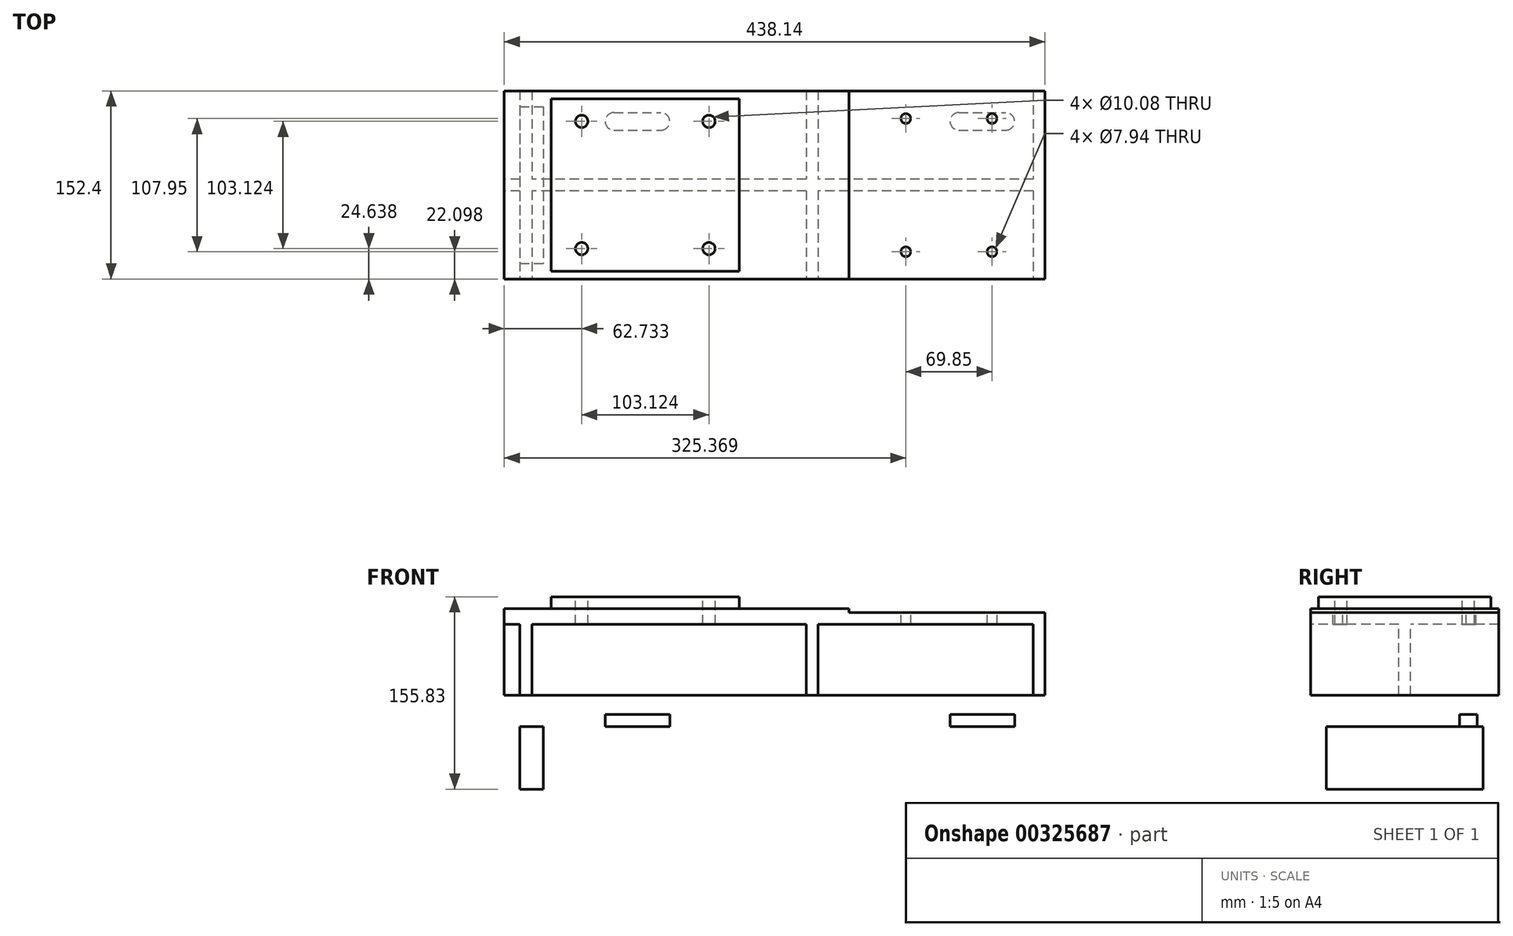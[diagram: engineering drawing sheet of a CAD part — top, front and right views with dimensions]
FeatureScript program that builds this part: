
annotation { "Feature Type Name" : "Feature", "Feature Type Description" : "" }
export const myFeature = defineFeature(function(context is Context, id is Id, definition is map)
    precondition{}
    {
        {
            var Q0;
            Q0=qCreatedBy(makeId("Top.planeOp"),FACE);
            var sketch = newSketch(context, id + "F0", { "sketchPlane" : qUnion([Q0])});
            skLineSegment(sketch, "E0.bottom", {"start": v(-219.08, 76.2) * mm, "end": v(219.08, 76.2) * mm});
            skLineSegment(sketch, "E0.top", {"start": v(-219.08, -76.2) * mm, "end": v(219.07, -76.2) * mm});
            skLineSegment(sketch, "E0.left", {"start": v(-219.08, 76.2) * mm, "end": v(-219.08, -76.2) * mm});
            skLineSegment(sketch, "E0.right", {"start": v(219.08, 76.2) * mm, "end": v(219.07, -76.2) * mm});
            skPoint(sketch, "E0.middle", {"position": v(0, 0) * mm});
            skSolve(sketch);
        }
        {
            var Q0;
            Q0=qSketchRegion(id+"F0",true);
            extrude(context, id + "F1", {"entities" : qUnion([Q0]), "oppositeDirection" : true, "depth" : 12.7 * mm});
        }
        {
            var Q0;
            Q0=makeQuery(id+"F1.opExtrude","CAP_FACE",FACE,{"disambiguationData":[OSD([sQuery(id+"F0.wireOp",EDGE,"E0.bottom"),sQuery(id+"F0.wireOp",EDGE,"E0.top"),sQuery(id+"F0.wireOp",EDGE,"E0.left"),sQuery(id+"F0.wireOp",EDGE,"E0.right")])],"isStart":true});
            var sketch = newSketch(context, id + "F2", { "sketchPlane" : qUnion([Q0])});
            skLineSegment(sketch, "E1.0", {"start": v(-104.78, 76.2) * mm, "end": v(-104.78, -76.2) * mm, "construction": true});
            skLineSegment(sketch, "E2.bottom", {"start": v(-180.98, -69.85) * mm, "end": v(-28.58, -69.85) * mm});
            skLineSegment(sketch, "E2.top", {"start": v(-180.98, 69.85) * mm, "end": v(-28.58, 69.85) * mm});
            skLineSegment(sketch, "E2.left", {"start": v(-180.98, -69.85) * mm, "end": v(-180.98, 69.85) * mm});
            skLineSegment(sketch, "E2.right", {"start": v(-28.58, -69.85) * mm, "end": v(-28.58, 69.85) * mm});
            skPoint(sketch, "E2.middle", {"position": v(-104.78, 0) * mm});
            skSolve(sketch);
        }
        {
            var Q0;
            Q0=qSketchRegion(id+"F2",true);
            extrude(context, id + "F3", {"entities" : qUnion([Q0]), "operationType" : NewBodyOperationType.ADD, "depth" : 9.52 * mm});
        }
        {
            var Q0;
            Q0=makeQuery(id+"F1.opExtrude","CAP_FACE",FACE,{"disambiguationData":[OSD([sQuery(id+"F0.wireOp",EDGE,"E0.bottom"),sQuery(id+"F0.wireOp",EDGE,"E0.top"),sQuery(id+"F0.wireOp",EDGE,"E0.left"),sQuery(id+"F0.wireOp",EDGE,"E0.right")])],"isStart":false});
            var sketch = newSketch(context, id + "F4", { "sketchPlane" : qUnion([Q0])});
            skLineSegment(sketch, "E3.0", {"start": v(-206.38, 76.2) * mm, "end": v(-196.72, 76.2) * mm});
            skLineSegment(sketch, "E4.0", {"start": v(-206.38, -76.2) * mm, "end": v(-196.72, -76.2) * mm});
            skLineSegment(sketch, "E5.0", {"start": v(-206.38, -76.2) * mm, "end": v(-206.38, 76.2) * mm});
            skLineSegment(sketch, "E6.0", {"start": v(-196.72, -76.2) * mm, "end": v(-196.72, 76.2) * mm});
            skLineSegment(sketch, "E7.0", {"start": v(25.53, -76.2) * mm, "end": v(25.53, 76.2) * mm});
            skLineSegment(sketch, "E8.0", {"start": v(35.18, -76.2) * mm, "end": v(35.18, 76.2) * mm});
            skLineSegment(sketch, "E9.0", {"start": v(219.08, -76.2) * mm, "end": v(219.07, 76.2) * mm});
            skLineSegment(sketch, "E10.0", {"start": v(209.42, -76.2) * mm, "end": v(209.42, 76.2) * mm});
            skLineSegment(sketch, "E11", {"start": v(219.08, 0) * mm, "end": v(-321.3, 0) * mm, "construction": true});
            skPoint(sketch, "E11.endSnap0", {"position": v(219.07, 0) * mm});
            skLineSegment(sketch, "E12.0", {"start": v(219.08, 4.76) * mm, "end": v(-219.08, 4.76) * mm});
            skLineSegment(sketch, "E13.MirrorCS", {"start": v(219.08, -4.76) * mm, "end": v(-219.08, -4.76) * mm});
            skLineSegment(sketch, "E14.0", {"start": v(-219.08, -4.76) * mm, "end": v(-219.08, 4.76) * mm});
            skPoint(sketch, "E15.orphan", {"position": v(-219.08, 76.2) * mm});
            skPoint(sketch, "E16.orphan", {"position": v(-321.3, 4.76) * mm});
            skPoint(sketch, "E17.orphan", {"position": v(-321.3, -4.76) * mm});
            skPoint(sketch, "E18.orphan", {"position": v(-219.08, -76.2) * mm});
            skLineSegment(sketch, "E19.trimOffspring", {"start": v(25.53, -76.2) * mm, "end": v(35.18, -76.2) * mm});
            skLineSegment(sketch, "E20.trimOffspring", {"start": v(25.53, 76.2) * mm, "end": v(35.18, 76.2) * mm});
            skLineSegment(sketch, "E21.trimOffspring", {"start": v(209.42, 76.2) * mm, "end": v(219.07, 76.2) * mm});
            skLineSegment(sketch, "E22.trimOffspring", {"start": v(209.42, -76.2) * mm, "end": v(219.08, -76.2) * mm});
            skSolve(sketch);
        }
        {
            var Q0;
            Q0=qSketchRegion(id+"F4",true);
            extrude(context, id + "F5", {"entities" : qUnion([Q0]), "operationType" : NewBodyOperationType.ADD, "depth" : 73.15 * mm});
        }
        {
            var Q0;
            Q0=makeQuery(id+"F5.opExtrude","CAP_FACE",FACE,{"disambiguationData":[OSD([sQuery(id+"F4.wireOp",EDGE,"E3.0"),sQuery(id+"F4.wireOp",EDGE,"E4.0"),sQuery(id+"F4.wireOp",EDGE,"E5.0"),sQuery(id+"F4.wireOp",EDGE,"E6.0"),sQuery(id+"F4.wireOp",EDGE,"E7.0"),sQuery(id+"F4.wireOp",EDGE,"E8.0"),sQuery(id+"F4.wireOp",EDGE,"E9.0"),sQuery(id+"F4.wireOp",EDGE,"E10.0"),sQuery(id+"F4.wireOp",EDGE,"E12.0"),sQuery(id+"F4.wireOp",EDGE,"E13.MirrorCS"),sQuery(id+"F4.wireOp",EDGE,"E14.0"),sQuery(id+"F4.wireOp",EDGE,"E19.trimOffspring"),sQuery(id+"F4.wireOp",EDGE,"E20.trimOffspring"),sQuery(id+"F4.wireOp",EDGE,"E21.trimOffspring"),sQuery(id+"F4.wireOp",EDGE,"E22.trimOffspring")])],"isStart":false});
            var sketch = newSketch(context, id + "F6", { "sketchPlane" : qUnion([Q0])});
            skLineSegment(sketch, "E23.0", {"start": v(-219.08, 76.2) * mm, "end": v(219.07, 76.2) * mm});
            skLineSegment(sketch, "E24.0", {"start": v(-219.08, -76.2) * mm, "end": v(-219.08, 76.2) * mm});
            skLineSegment(sketch, "E25.0", {"start": v(-219.08, -76.2) * mm, "end": v(219.08, -76.2) * mm});
            skLineSegment(sketch, "E26.0", {"start": v(219.08, -76.2) * mm, "end": v(219.07, 76.2) * mm});
            skPoint(sketch, "E27.orphan", {"position": v(-219.08, -4.76) * mm});
            skPoint(sketch, "E28.orphan", {"position": v(-196.72, 76.2) * mm});
            skPoint(sketch, "E29.orphan", {"position": v(25.53, 76.2) * mm});
            skPoint(sketch, "E30.orphan", {"position": v(-196.72, -76.2) * mm});
            skPoint(sketch, "E31.orphan", {"position": v(25.53, -76.2) * mm});
            skSolve(sketch);
        }
        {
            var Q0;
            Q0=qSketchRegion(id+"F6",true);
            extrude(context, id + "F7", {"entities" : qUnion([Q0]), "operationType" : NewBodyOperationType.ADD, "depth" : 9.65 * mm});
        }
        {
            var Q0;
            Q0=makeQuery(id+"F7.opExtrude","CAP_FACE",FACE,{"disambiguationData":[OSD([sQuery(id+"F6.wireOp",EDGE,"E23.0"),sQuery(id+"F6.wireOp",EDGE,"E24.0"),sQuery(id+"F6.wireOp",EDGE,"E25.0"),sQuery(id+"F6.wireOp",EDGE,"E26.0")])],"isStart":false});
            var sketch = newSketch(context, id + "F8", { "sketchPlane" : qUnion([Q0])});
            skLineSegment(sketch, "E32", {"start": v(-219.08, 0) * mm, "end": v(219.07, 0) * mm, "construction": true});
            skLineSegment(sketch, "E33.0", {"start": v(-130.18, -76.2) * mm, "end": v(-130.18, 76.2) * mm, "construction": true});
            skLineSegment(sketch, "E34.0", {"start": v(-92.08, -76.2) * mm, "end": v(-92.08, 76.2) * mm, "construction": true});
            skLineSegment(sketch, "E35.0", {"start": v(149.22, -76.2) * mm, "end": v(149.22, 76.2) * mm, "construction": true});
            skLineSegment(sketch, "E36.0", {"start": v(187.32, -76.2) * mm, "end": v(187.32, 76.2) * mm, "construction": true});
            skLineSegment(sketch, "E37.0", {"start": v(-130.18, -51.56) * mm, "end": v(-92.08, -51.56) * mm});
            skLineSegment(sketch, "E38.trimOffspring", {"start": v(149.22, -51.56) * mm, "end": v(187.32, -51.56) * mm});
            skArc(sketch, "E39.0.startCap", {"start": v(-130.18, -58.67) * mm, "mid": v(-137.29, -51.56) * mm, "end": v(-130.18, -44.45) * mm});
            skArc(sketch, "E39.0.endCap", {"start": v(-92.08, -44.45) * mm, "mid": v(-84.96, -51.56) * mm, "end": v(-92.08, -58.67) * mm});
            skLineSegment(sketch, "E39.0.left", {"start": v(-130.18, -44.45) * mm, "end": v(-92.08, -44.45) * mm});
            skLineSegment(sketch, "E39.0.right", {"start": v(-130.18, -58.67) * mm, "end": v(-92.08, -58.67) * mm});
            skArc(sketch, "E39.1.startCap", {"start": v(149.22, -58.67) * mm, "mid": v(142.11, -51.56) * mm, "end": v(149.22, -44.45) * mm});
            skArc(sketch, "E39.1.endCap", {"start": v(187.32, -44.45) * mm, "mid": v(194.44, -51.56) * mm, "end": v(187.32, -58.67) * mm});
            skLineSegment(sketch, "E39.1.left", {"start": v(149.22, -44.45) * mm, "end": v(187.32, -44.45) * mm});
            skLineSegment(sketch, "E39.1.right", {"start": v(149.22, -58.67) * mm, "end": v(187.32, -58.67) * mm});
            skArc(sketch, "E40.MirrorCS", {"start": v(-92.08, 44.45) * mm, "mid": v(-84.96, 51.56) * mm, "end": v(-92.08, 58.67) * mm});
            skArc(sketch, "E41.MirrorCS", {"start": v(-130.18, 58.67) * mm, "mid": v(-137.29, 51.56) * mm, "end": v(-130.18, 44.45) * mm});
            skLineSegment(sketch, "E42.MirrorCS", {"start": v(149.22, 51.56) * mm, "end": v(187.32, 51.56) * mm});
            skLineSegment(sketch, "E43.MirrorCS", {"start": v(-130.18, 51.56) * mm, "end": v(-92.08, 51.56) * mm});
            skLineSegment(sketch, "E44.MirrorCS", {"start": v(149.22, 58.67) * mm, "end": v(187.32, 58.67) * mm});
            skLineSegment(sketch, "E45.MirrorCS", {"start": v(-130.18, 44.45) * mm, "end": v(-92.08, 44.45) * mm});
            skLineSegment(sketch, "E46.MirrorCS", {"start": v(149.22, 44.45) * mm, "end": v(187.32, 44.45) * mm});
            skArc(sketch, "E47.MirrorCS", {"start": v(149.22, 58.67) * mm, "mid": v(142.11, 51.56) * mm, "end": v(149.22, 44.45) * mm});
            skArc(sketch, "E48.MirrorCS", {"start": v(187.32, 44.45) * mm, "mid": v(194.44, 51.56) * mm, "end": v(187.32, 58.67) * mm});
            skLineSegment(sketch, "E49.MirrorCS", {"start": v(-130.18, 58.67) * mm, "end": v(-92.08, 58.67) * mm});
            skSolve(sketch);
        }
        {
            var Q0;
            Q0=makeQuery(id+"F8.imprint","IMPRINT",FACE,{"disambiguationData":[TD([[makeQuery(id+"F8.imprint","IMPRINT",EDGE,{"derivedFrom":sQuery(id+"F8.wireOp",EDGE,"E40.MirrorCS")}),1.0]])]});
            var Q1;
            Q1=makeQuery(id+"F8.imprint","IMPRINT",FACE,{"disambiguationData":[TD([[makeQuery(id+"F8.imprint","IMPRINT",EDGE,{"derivedFrom":sQuery(id+"F8.wireOp",EDGE,"E39.0.startCap")}),-1.0]])]});
            var Q2;
            Q2=makeQuery(id+"F8.imprint","IMPRINT",FACE,{"disambiguationData":[TD([[makeQuery(id+"F8.imprint","IMPRINT",EDGE,{"derivedFrom":sQuery(id+"F8.wireOp",EDGE,"E44.MirrorCS")}),-1.0]])]});
            var Q3;
            Q3=makeQuery(id+"F8.imprint","IMPRINT",FACE,{"disambiguationData":[TD([[makeQuery(id+"F8.imprint","IMPRINT",EDGE,{"derivedFrom":sQuery(id+"F8.wireOp",EDGE,"E39.1.startCap")}),-1.0]])]});
            extrude(context, id + "F9", {"entities" : qUnion([Q0, Q1, Q2, Q3]), "operationType" : NewBodyOperationType.REMOVE, "oppositeDirection" : true, "depth" : 25.4 * mm});
        }
        {
            var Q0;
            Q0=makeQuery(id+"F3.opExtrude","CAP_FACE",FACE,{"disambiguationData":[OSD([sQuery(id+"F2.wireOp",EDGE,"E2.bottom"),sQuery(id+"F2.wireOp",EDGE,"E2.top"),sQuery(id+"F2.wireOp",EDGE,"E2.left"),sQuery(id+"F2.wireOp",EDGE,"E2.right")])],"isStart":false});
            var sketch = newSketch(context, id + "F10", { "sketchPlane" : qUnion([Q0])});
            skLineSegment(sketch, "E50.0", {"start": v(-180.98, 69.85) * mm, "end": v(-28.58, 69.85) * mm, "construction": true});
            skLineSegment(sketch, "E51.0", {"start": v(-180.98, -69.85) * mm, "end": v(-180.98, 69.85) * mm, "construction": true});
            skLineSegment(sketch, "E52.0", {"start": v(-180.98, -69.85) * mm, "end": v(-28.58, -69.85) * mm, "construction": true});
            skLineSegment(sketch, "E53", {"start": v(-28.58, -69.85) * mm, "end": v(-180.97, 69.85) * mm, "construction": true});
            skLineSegment(sketch, "E54.bottom", {"start": v(-156.34, 51.56) * mm, "end": v(-53.21, 51.56) * mm, "construction": true});
            skLineSegment(sketch, "E54.top", {"start": v(-156.34, -51.56) * mm, "end": v(-53.21, -51.56) * mm, "construction": true});
            skLineSegment(sketch, "E54.left", {"start": v(-156.34, 51.56) * mm, "end": v(-156.34, -51.56) * mm, "construction": true});
            skLineSegment(sketch, "E54.right", {"start": v(-53.21, 51.56) * mm, "end": v(-53.21, -51.56) * mm, "construction": true});
            skPoint(sketch, "E54.middle", {"position": v(-104.78, 0) * mm});
            skPoint(sketch, "E55", {"position": v(-156.34, 51.56) * mm});
            skPoint(sketch, "E56", {"position": v(-53.21, 51.56) * mm});
            skPoint(sketch, "E57", {"position": v(-156.34, -51.56) * mm});
            skPoint(sketch, "E58", {"position": v(-53.21, -51.56) * mm});
            skSolve(sketch);
        }
        {
            var Q0;
            Q0=sQuery(id+"F10.wireOp",VERTEX,"E55");
            var Q1;
            Q1=sQuery(id+"F10.wireOp",VERTEX,"E56");
            var Q2;
            Q2=sQuery(id+"F10.wireOp",VERTEX,"E57");
            var Q3;
            Q3=sQuery(id+"F10.wireOp",VERTEX,"E58");
            var Q4;
            Q4=makeQuery(id+"F1.opExtrude","SWEPT_BODY",BODY,{"disambiguationData":[OSD([sQuery(id+"F0.wireOp",EDGE,"E0.bottom"),sQuery(id+"F0.wireOp",EDGE,"E0.top"),sQuery(id+"F0.wireOp",EDGE,"E0.left"),sQuery(id+"F0.wireOp",EDGE,"E0.right")])]});
            hole(context, id + "F11", {"style" : HoleStyle.SIMPLE, "endStyle" : HoleEndStyle.BLIND, "standardTappedOrClearance" : lookupTablePath({ "standard" : "ANSI", "fit" : "Normal (ASME)", "size" : "3/8", "type" : "Clearance" }), "standardBlindInLast" : lookupTablePath({ "fit" : "Free", "standard" : "ANSI", "size" : "3/8", "type" : "Clearance" }), "holeDiameter" : 10.08 * mm, "holeDepth" : 38.1 * mm, "tappedDepth" : 14.3 * mm, "tapClearance" : 3, "locations" : qUnion([Q0, Q1, Q2, Q3]), "scope" : qUnion([Q4])});
        }
        {
            var Q0;
            Q0=makeQuery(id+"F1.opExtrude","CAP_FACE",FACE,{"disambiguationData":[OSD([sQuery(id+"F0.wireOp",EDGE,"E0.bottom"),sQuery(id+"F0.wireOp",EDGE,"E0.top"),sQuery(id+"F0.wireOp",EDGE,"E0.left"),sQuery(id+"F0.wireOp",EDGE,"E0.right")])],"isStart":true});
            var sketch = newSketch(context, id + "F12", { "sketchPlane" : qUnion([Q0])});
            skLineSegment(sketch, "E59.bottom", {"start": v(219.08, 76.2) * mm, "end": v(60.33, 76.2) * mm});
            skLineSegment(sketch, "E59.top", {"start": v(219.08, -76.2) * mm, "end": v(60.33, -76.2) * mm});
            skLineSegment(sketch, "E59.left", {"start": v(219.08, 76.2) * mm, "end": v(219.08, -76.2) * mm});
            skLineSegment(sketch, "E59.right", {"start": v(60.33, 76.2) * mm, "end": v(60.33, -76.2) * mm});
            skSolve(sketch);
        }
        {
            var Q0;
            Q0=qSketchRegion(id+"F12",true);
            extrude(context, id + "F13", {"entities" : qUnion([Q0]), "operationType" : NewBodyOperationType.REMOVE, "oppositeDirection" : true, "depth" : 3.17 * mm});
        }
        {
            var Q0;
            Q0=makeQuery(id+"F13.boolean.opBoolean","COPY",FACE,{"derivedFrom":makeQuery(id+"F13.opExtrude","CAP_FACE",FACE,{"disambiguationData":[OSD([sQuery(id+"F12.wireOp",EDGE,"E59.bottom"),sQuery(id+"F12.wireOp",EDGE,"E59.top"),sQuery(id+"F12.wireOp",EDGE,"E59.left"),sQuery(id+"F12.wireOp",EDGE,"E59.right")])],"isStart":false})});
            var sketch = newSketch(context, id + "F14", { "sketchPlane" : qUnion([Q0])});
            skLineSegment(sketch, "E60.0", {"start": v(-180.98, 69.85) * mm, "end": v(-28.58, 69.85) * mm, "construction": true});
            skLineSegment(sketch, "E61", {"start": v(-104.78, 69.85) * mm, "end": v(-104.78, -100.76) * mm, "construction": true});
            skLineSegment(sketch, "E62.0", {"start": v(219.08, 76.2) * mm, "end": v(219.07, -76.2) * mm, "construction": true});
            skLineSegment(sketch, "E63", {"start": v(219.07, 0) * mm, "end": v(-246.08, 0) * mm, "construction": true});
            skLineSegment(sketch, "E64.0", {"start": v(141.35, 69.85) * mm, "end": v(141.35, -100.76) * mm, "construction": true});
            skLineSegment(sketch, "E65.0", {"start": v(106.3, 69.85) * mm, "end": v(106.3, -100.76) * mm, "construction": true});
            skLineSegment(sketch, "E66.0", {"start": v(219.07, 53.85) * mm, "end": v(-246.08, 53.85) * mm, "construction": true});
            skPoint(sketch, "E67", {"position": v(106.3, 53.85) * mm});
            skPoint(sketch, "E68.0.1.0", {"position": v(106.3, -54.1) * mm});
            skPoint(sketch, "E68.1.0.0", {"position": v(176.15, 53.85) * mm});
            skPoint(sketch, "E68.1.1.0", {"position": v(176.15, -54.1) * mm});
            skLineSegment(sketch, "E68.direction1", {"start": v(106.3, 53.85) * mm, "end": v(176.15, 53.85) * mm, "construction": true});
            skLineSegment(sketch, "E68.direction2", {"start": v(106.3, 53.85) * mm, "end": v(106.3, -54.1) * mm, "construction": true});
            skSolve(sketch);
        }
        {
            var Q0;
            Q0=sQuery(id+"F14.wireOp",VERTEX,"E67");
            var Q1;
            Q1=sQuery(id+"F14.wireOp",VERTEX,"E68.1.0.0");
            var Q2;
            Q2=sQuery(id+"F14.wireOp",VERTEX,"E68.1.1.0");
            var Q3;
            Q3=sQuery(id+"F14.wireOp",VERTEX,"E68.0.1.0");
            var Q4;
            Q4=makeQuery(id+"F1.opExtrude","SWEPT_BODY",BODY,{"disambiguationData":[OSD([sQuery(id+"F0.wireOp",EDGE,"E0.bottom"),sQuery(id+"F0.wireOp",EDGE,"E0.top"),sQuery(id+"F0.wireOp",EDGE,"E0.left"),sQuery(id+"F0.wireOp",EDGE,"E0.right")])]});
            hole(context, id + "F15", {"style" : HoleStyle.SIMPLE, "endStyle" : HoleEndStyle.BLIND, "holeDiameter" : 7.94 * mm, "holeDepth" : 38.1 * mm, "tappedDepth" : 14.3 * mm, "tapClearance" : 3, "locations" : qUnion([Q0, Q1, Q2, Q3]), "scope" : qUnion([Q4])});
        }
        {
            var Q0;
            Q0=makeQuery(id+"F7.opExtrude","CAP_FACE",FACE,{"disambiguationData":[OSD([sQuery(id+"F6.wireOp",EDGE,"E23.0"),sQuery(id+"F6.wireOp",EDGE,"E24.0"),sQuery(id+"F6.wireOp",EDGE,"E25.0"),sQuery(id+"F6.wireOp",EDGE,"E26.0")])],"isStart":false});
            var sketch = newSketch(context, id + "F16", { "sketchPlane" : qUnion([Q0])});
            skLineSegment(sketch, "E69.0", {"start": v(-206.38, -63.5) * mm, "end": v(-206.38, 63.5) * mm});
            skLineSegment(sketch, "E70.0", {"start": v(-187.33, -63.5) * mm, "end": v(-187.33, 63.5) * mm});
            skLineSegment(sketch, "E71", {"start": v(-219.08, 0) * mm, "end": v(-163.17, 0) * mm, "construction": true});
            skPoint(sketch, "E71.endSnap0", {"position": v(-219.08, 0) * mm});
            skLineSegment(sketch, "E72.0", {"start": v(-206.38, -63.5) * mm, "end": v(-187.33, -63.5) * mm});
            skLineSegment(sketch, "E73.MirrorCS", {"start": v(-206.38, 63.5) * mm, "end": v(-187.33, 63.5) * mm});
            skPoint(sketch, "E74.orphan", {"position": v(-219.08, 63.5) * mm});
            skPoint(sketch, "E75.orphan", {"position": v(-163.17, 63.5) * mm});
            skPoint(sketch, "E76.orphan", {"position": v(-163.17, -63.5) * mm});
            skPoint(sketch, "E77.orphan", {"position": v(-219.08, -63.5) * mm});
            skSolve(sketch);
        }
        {
            var Q0;
            Q0=qSketchRegion(id+"F16",true);
            extrude(context, id + "F17", {"entities" : qUnion([Q0]), "operationType" : NewBodyOperationType.ADD, "depth" : 50.8 * mm});
        }
        {
            var Q0;
            Q0=makeQuery(id+"F17.opExtrude","SWEPT_FACE",FACE,{"disambiguationData":[OSD([sQuery(id+"F16.wireOp",EDGE,"E69.0")])]});
            var sketch = newSketch(context, id + "F18", { "sketchPlane" : qUnion([Q0])});
            skLineSegment(sketch, "E78.0", {"start": v(-76.2, -127.25) * mm, "end": v(76.2, -127.25) * mm, "construction": true});
            skLineSegment(sketch, "E79", {"start": v(0, -146.3) * mm, "end": v(0, -111.54) * mm, "construction": true});
            skPoint(sketch, "E79.endSnap0", {"position": v(0, -127.25) * mm});
            skLineSegment(sketch, "E80.0", {"start": v(50.8, -146.3) * mm, "end": v(50.8, -111.54) * mm, "construction": true});
            skPoint(sketch, "E81", {"position": v(50.8, -127.25) * mm});
            skPoint(sketch, "E82.MirrorP", {"position": v(-50.8, -127.25) * mm});
            skSolve(sketch);
        }
        {
            var Q0;
            Q0=sQuery(id+"F18.wireOp",VERTEX,"E81");
            var Q1;
            Q1=sQuery(id+"F18.wireOp",VERTEX,"E82.MirrorP");
            var Q2;
            Q2=makeQuery(id+"F1.opExtrude","SWEPT_BODY",BODY,{"disambiguationData":[OSD([sQuery(id+"F0.wireOp",EDGE,"E0.bottom"),sQuery(id+"F0.wireOp",EDGE,"E0.top"),sQuery(id+"F0.wireOp",EDGE,"E0.left"),sQuery(id+"F0.wireOp",EDGE,"E0.right")])]});
            hole(context, id + "F19", {"style" : HoleStyle.SIMPLE, "endStyle" : HoleEndStyle.BLIND, "standardTappedOrClearance" : lookupTablePath({ "standard" : "ANSI", "engagement" : "75%", "pitch" : "11 tpi", "size" : "5/8", "type" : "Tapped" }), "standardBlindInLast" : lookupTablePath({ "standard" : "ANSI", "engagement" : "75%", "pitch" : "11 tpi", "size" : "5/8", "type" : "Tapped" }), "holeDiameter" : 13.5 * mm, "showTappedDepth" : true, "holeDepth" : 21.23 * mm, "tappedDepth" : 14.3 * mm, "tapClearance" : 3, "locations" : qUnion([Q0, Q1]), "scope" : qUnion([Q2]), "majorDiameter" : 15.88 * mm});
        }
    });
